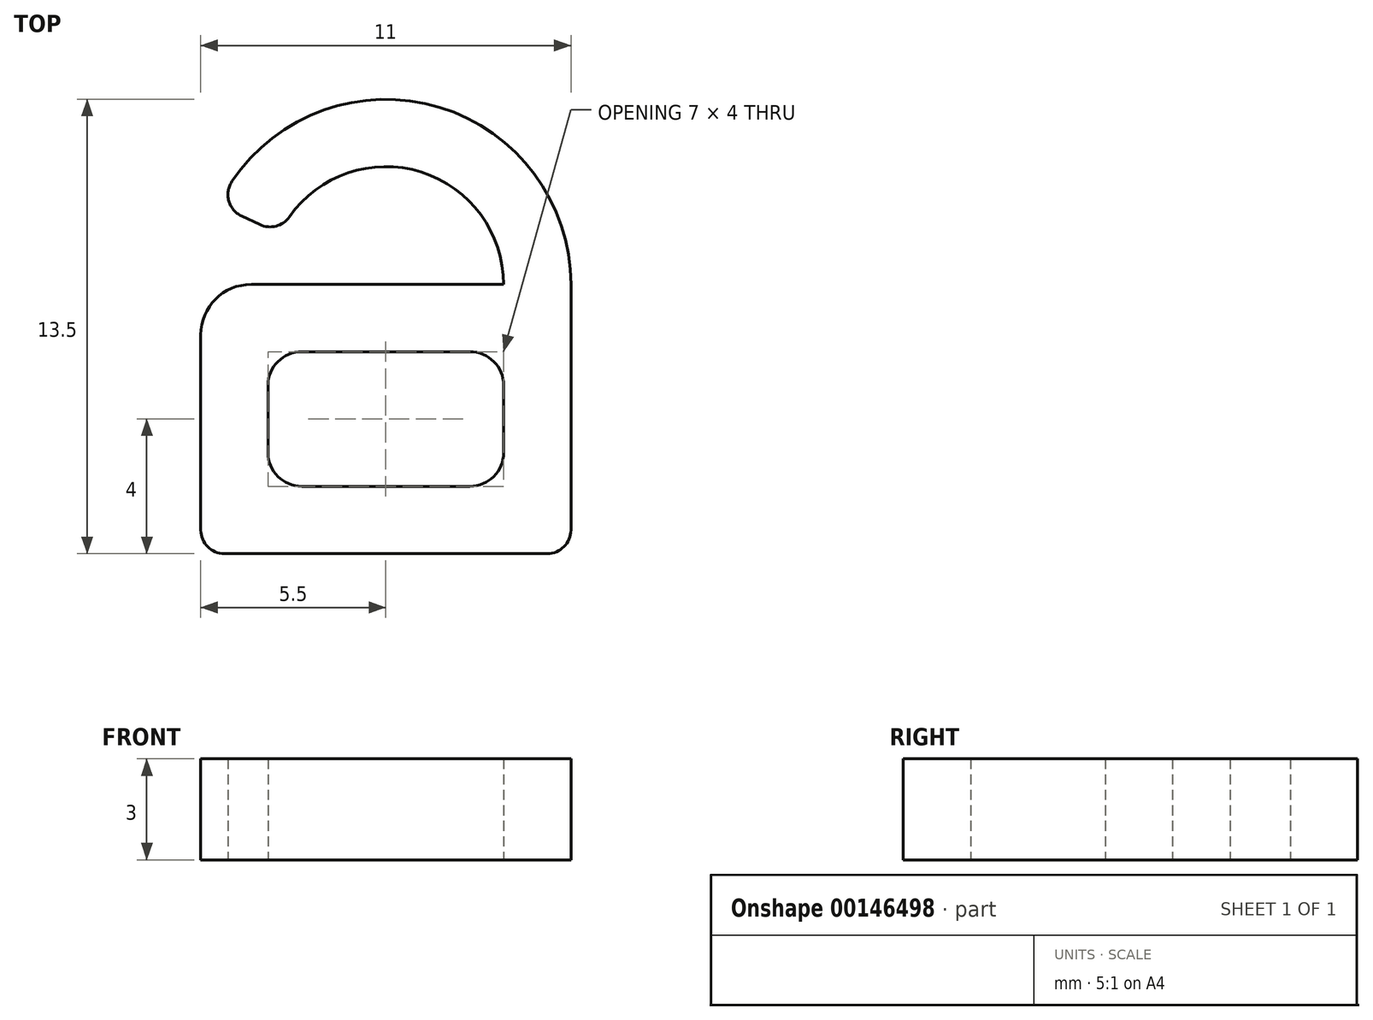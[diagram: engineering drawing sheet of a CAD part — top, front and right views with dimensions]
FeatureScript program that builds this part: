
annotation { "Feature Type Name" : "Feature", "Feature Type Description" : "" }
export const myFeature = defineFeature(function(context is Context, id is Id, definition is map)
    precondition{}
    {
        {
            var Q0;
            Q0=qCreatedBy(makeId("Top.planeOp"),FACE);
            var sketch = newSketch(context, id + "F0", { "sketchPlane" : qUnion([Q0])});
            skLineSegment(sketch, "E0", {"start": v(-4, 0) * mm, "end": v(3.5, 0) * mm});
            skArc(sketch, "E1", {"start": v(5.5, 0) * mm, "mid": v(1.6, 5.26) * mm, "end": v(-4.57, 3.06) * mm});
            skLineSegment(sketch, "E2", {"start": v(-4.3, 2.04) * mm, "end": v(-3.74, 1.77) * mm});
            skArc(sketch, "E3", {"start": v(-2.87, 2) * mm, "mid": v(1.05, 3.34) * mm, "end": v(3.5, 0) * mm});
            skPoint(sketch, "E4", {"position": v(0, 3.5) * mm});
            skLineSegment(sketch, "E5", {"start": v(-5.5, -1.5) * mm, "end": v(-5.5, -7.3) * mm});
            skLineSegment(sketch, "E6", {"start": v(-4.8, -8) * mm, "end": v(4.8, -8) * mm});
            skLineSegment(sketch, "E7", {"start": v(5.5, -7.3) * mm, "end": v(5.5, 0) * mm});
            skLineSegment(sketch, "E8.0", {"start": v(-2.5, -6) * mm, "end": v(2.5, -6) * mm});
            skLineSegment(sketch, "E8.1", {"start": v(-3.5, -3) * mm, "end": v(-3.5, -5) * mm});
            skLineSegment(sketch, "E8.2", {"start": v(-2.5, -2) * mm, "end": v(2.5, -2) * mm});
            skLineSegment(sketch, "E8.3", {"start": v(3.5, -5) * mm, "end": v(3.5, -3) * mm});
            skPoint(sketch, "E9.visualSharp", {"position": v(-5.5, -8) * mm});
            skArc(sketch, "E9.filletArc", {"start": v(-5.5, -7.3) * mm, "mid": v(-5.3, -7.8) * mm, "end": v(-4.8, -8) * mm});
            skPoint(sketch, "E10.visualSharp", {"position": v(5.5, -8) * mm});
            skArc(sketch, "E10.filletArc", {"start": v(4.8, -8) * mm, "mid": v(5.3, -7.8) * mm, "end": v(5.5, -7.3) * mm});
            skPoint(sketch, "E11.visualSharp", {"position": v(-3.16, 1.5) * mm});
            skArc(sketch, "E11.filletArc", {"start": v(-3.74, 1.77) * mm, "mid": v(-3.26, 1.73) * mm, "end": v(-2.87, 2) * mm});
            skPoint(sketch, "E12.visualSharp", {"position": v(-4.97, 2.36) * mm});
            skArc(sketch, "E12.filletArc", {"start": v(-4.57, 3.06) * mm, "mid": v(-4.67, 2.48) * mm, "end": v(-4.3, 2.04) * mm});
            skPoint(sketch, "E13.visualSharp", {"position": v(-5.5, 0) * mm});
            skArc(sketch, "E13.filletArc", {"start": v(-4, 0) * mm, "mid": v(-5.06, -0.44) * mm, "end": v(-5.5, -1.5) * mm});
            skPoint(sketch, "E14.visualSharp", {"position": v(-3.5, -2) * mm});
            skArc(sketch, "E14.filletArc", {"start": v(-2.5, -2) * mm, "mid": v(-3.2, -2.3) * mm, "end": v(-3.5, -3) * mm});
            skPoint(sketch, "E15.visualSharp", {"position": v(-3.5, -6) * mm});
            skArc(sketch, "E15.filletArc", {"start": v(-3.5, -5) * mm, "mid": v(-3.2, -5.7) * mm, "end": v(-2.5, -6) * mm});
            skPoint(sketch, "E16.visualSharp", {"position": v(3.5, -6) * mm});
            skArc(sketch, "E16.filletArc", {"start": v(2.5, -6) * mm, "mid": v(3.2, -5.7) * mm, "end": v(3.5, -5) * mm});
            skPoint(sketch, "E17.visualSharp", {"position": v(3.5, -2) * mm});
            skArc(sketch, "E17.filletArc", {"start": v(3.5, -3) * mm, "mid": v(3.2, -2.3) * mm, "end": v(2.5, -2) * mm});
            skSolve(sketch);
        }
        {
            var Q0;
            Q0=makeQuery(id+"F0.imprint","IMPRINT",FACE,{"disambiguationData":[TD([[makeQuery(id+"F0.imprint","IMPRINT",EDGE,{"derivedFrom":sQuery(id+"F0.wireOp",EDGE,"E0")}),-1.0]])]});
            extrude(context, id + "F1", {"entities" : qUnion([Q0]), "depth" : 3 * mm});
        }
    });
